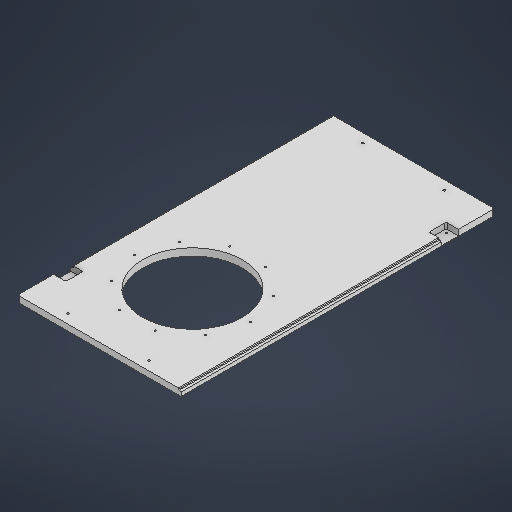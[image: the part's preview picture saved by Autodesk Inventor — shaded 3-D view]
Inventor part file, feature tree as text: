
AUTODESK INVENTOR PART (.ipt)
format: ipt  version: 2025 (Build 290162000, 162)  size: 330,240 bytes
history: native  units: in
note: dims shown in document units (in); Inventor stores cm internally (conversion verified against a paired STEP export)
features: sketch x9, chamfer x5, extrude x4, hole x3, plane x2, fillet x1
ambient origin geometry x8: Origin, YZ Plane, XZ Plane, XY Plane, X Axis, Y Axis, Z Axis, Center Point
bodies: Solid1 (feature_tree)
feature tree (24):
  extrude  "Extrusion1"  Depth=27.1654in
  sketch  "Sketch2"  dims[d2=0.625in d3=0.0in d4=8.0709in]
  extrude  "Extrusion2"  Depth=0.625in
  plane  "Work Plane1"
  hole  "Hole3"  [1 undecoded]
  sketch  "Sketch7"  dims[d56=25.5906in]
  plane  "Work Plane2"
  hole  "Hole4"  [1 undecoded]
  sketch  "Sketch9"  dims[d64=10.3543in]
  fillet  "Fillet2"  Radius=7.0625in
  chamfer  "Chamfer1"  Distance=0.1575in
  chamfer  "Chamfer2"  Distance=3.937in Angle=360.0deg
  extrude  "Extrusion7"  Depth=1.063in
  extrude  "Extrusion8"  Depth=1.063in
  chamfer  "Chamfer3"  Distance=1.4961in
  chamfer  "Chamfer4"  Distance=1.4961in
  hole  "Hole5"  [1 undecoded]
  chamfer  "Chamfer5"  Distance=3.1102in
  sketch  "Sketch1"  dims[d0=14.1732in d1=27.1654in]
  sketch  "Sketch6"  dims[d8=10.6299in d50=5.9055in d55=7.0625in]
  sketch  "Sketch8"  dims[d57=0.1936in d58=0.1969in d59=0.1575in d60=0.0787in d61=90.0deg d62=0.1969in d63=0.8108in]
  sketch  "Sketch Circular Pattern4"  dims[d5=8.6614in d6=0.0in d7=0.0in]
  sketch  "Sketch10"  dims[d65=10.6299in]
  sketch  "Sketch11"  dims[d68=10.0394in d69=0.1575in d70=3.937in d72=360.0deg d74=0.1628in d75=0.3937in d76=0.1575in d77=0.0787in d78=90.0deg d79=0.3937in d80=0.8108in d82=1.063in d83=1.063in d84=1.4961in d85=1.4961in d86=3.1102in d87=3.1102in d88=0.1969in d89=0.0984in d90=0.0787in d91=45.0deg d92=0.0984in d93=0.0787in d94=45.0deg d95=0.1181in d96=0.1181in d97=0.4951in d98=0.0in d99=0.2362in d100=0.2362in d101=0.122in d102=0.0in d103=0.0787in d104=0.1378in d105=45.0deg d106=0.1378in d107=0.0787in d108=45.0deg d109=0.748in d110=0.315in d111=0.8661in d112=0.748in d113=0.1299in d114=0.1299in d115=0.1299in d116=0.1299in d118=0.315in d119=0.8661in d120=0.748in d121=0.748in d122=0.1276in d123=0.315in d124=0.1575in d125=0.0787in d126=90.0deg d127=0.315in d128=0.8108in d129=0.0138in d130=0.0787in d131=45.0deg d26=0.0394in d27=0.0394in d28=0.0394in d29=0.0059in d30=0.0098in d31=0.0148in d32=0.5635in d33=0.0295in d34=0.8108in d35=0.0025in d36=0.0295in d37=0.0148in d66=0.0197in d67=0.0344in]
note: 3 required parameter values undecoded (feature->parameter linkage not recoverable at this tier; creation-order binding heuristic only, values carry confidence <= 0.55)
